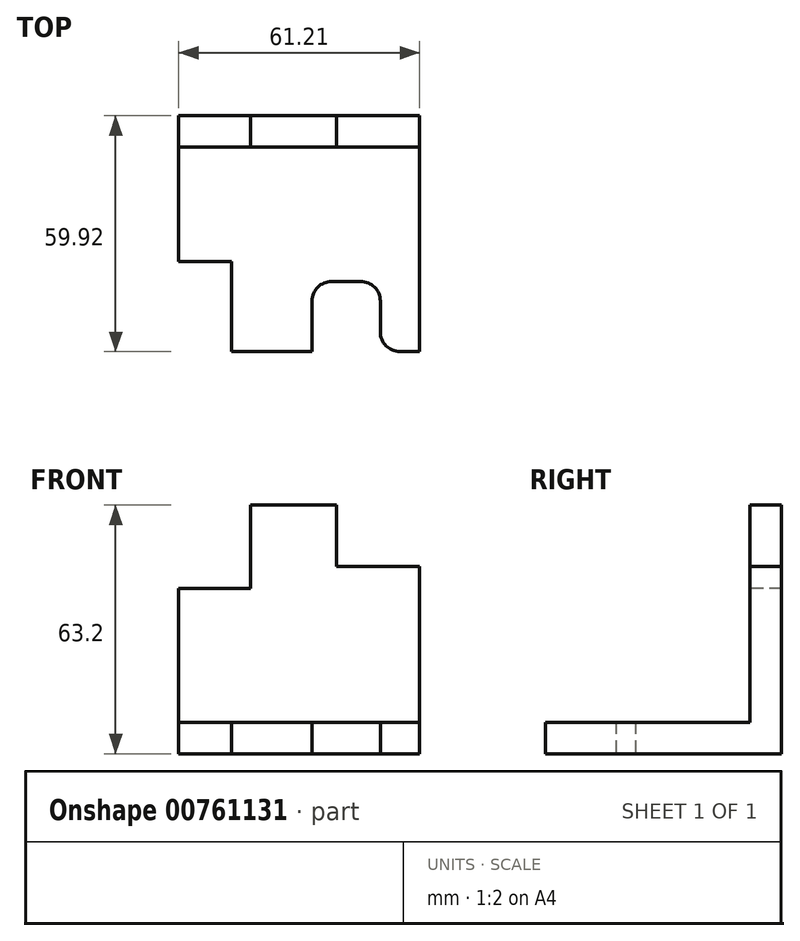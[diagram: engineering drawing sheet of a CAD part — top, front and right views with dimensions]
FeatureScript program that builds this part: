
annotation { "Feature Type Name" : "Feature", "Feature Type Description" : "" }
export const myFeature = defineFeature(function(context is Context, id is Id, definition is map)
    precondition{}
    {
        {
            var Q0;
            Q0=qCreatedBy(makeId("Top.planeOp"),FACE);
            var sketch = newSketch(context, id + "F0", { "sketchPlane" : qUnion([Q0])});
            skLineSegment(sketch, "E0", {"start": v(0, 0) * mm, "end": v(0, -29.06) * mm});
            skLineSegment(sketch, "E1", {"start": v(0, -29.06) * mm, "end": v(13.43, -29.06) * mm});
            skLineSegment(sketch, "E2", {"start": v(13.43, -29.06) * mm, "end": v(13.43, -51.92) * mm});
            skLineSegment(sketch, "E3", {"start": v(13.43, -51.92) * mm, "end": v(33.86, -51.92) * mm});
            skLineSegment(sketch, "E4", {"start": v(33.86, -51.92) * mm, "end": v(33.86, -39.1) * mm});
            skLineSegment(sketch, "E5", {"start": v(38.86, -34.1) * mm, "end": v(46.22, -34.1) * mm});
            skLineSegment(sketch, "E6", {"start": v(51.22, -39.1) * mm, "end": v(51.22, -46.92) * mm});
            skLineSegment(sketch, "E7", {"start": v(56.22, -51.92) * mm, "end": v(61.2, -51.92) * mm});
            skLineSegment(sketch, "E8", {"start": v(61.2, -51.92) * mm, "end": v(61.2, 0) * mm});
            skLineSegment(sketch, "E9", {"start": v(61.2, 0) * mm, "end": v(0, 0) * mm});
            skPoint(sketch, "E10.visualSharp", {"position": v(51.22, -34.1) * mm});
            skArc(sketch, "E10.filletArc", {"start": v(51.22, -39.1) * mm, "mid": v(49.76, -35.57) * mm, "end": v(46.22, -34.1) * mm});
            skPoint(sketch, "E11.visualSharp", {"position": v(33.86, -34.1) * mm});
            skArc(sketch, "E11.filletArc", {"start": v(38.86, -34.1) * mm, "mid": v(35.33, -35.57) * mm, "end": v(33.86, -39.1) * mm});
            skPoint(sketch, "E12.visualSharp", {"position": v(51.22, -51.92) * mm});
            skArc(sketch, "E12.filletArc", {"start": v(51.22, -46.92) * mm, "mid": v(52.69, -50.46) * mm, "end": v(56.22, -51.92) * mm});
            skSolve(sketch);
        }
        {
            var Q0;
            Q0=makeQuery(id+"F0.imprint","IMPRINT",FACE,{"disambiguationData":[TD([[makeQuery(id+"F0.imprint","IMPRINT",EDGE,{"derivedFrom":sQuery(id+"F0.wireOp",EDGE,"E0")}),1.0]])]});
            extrude(context, id + "F1", {"entities" : qUnion([Q0]), "depth" : 8 * mm, "offsetDistance" : 25 * mm});
        }
        {
            var Q0;
            Q0=qCreatedBy(makeId("Front.planeOp"),FACE);
            var sketch = newSketch(context, id + "F2", { "sketchPlane" : qUnion([Q0])});
            skLineSegment(sketch, "E13", {"start": v(0, 42) * mm, "end": v(18.28, 42) * mm});
            skLineSegment(sketch, "E14", {"start": v(18.28, 42) * mm, "end": v(18.28, 63.2) * mm});
            skLineSegment(sketch, "E15", {"start": v(18.28, 63.2) * mm, "end": v(40.03, 63.2) * mm});
            skLineSegment(sketch, "E16", {"start": v(40.03, 63.2) * mm, "end": v(40.03, 47.55) * mm});
            skLineSegment(sketch, "E17", {"start": v(40.03, 47.55) * mm, "end": v(61.2, 47.55) * mm});
            skLineSegment(sketch, "E18", {"start": v(61.2, 47.55) * mm, "end": v(61.2, 0) * mm});
            skLineSegment(sketch, "E19", {"start": v(61.2, 0) * mm, "end": v(0, 0) * mm});
            skLineSegment(sketch, "E20", {"start": v(0, 0) * mm, "end": v(0, 42) * mm});
            skSolve(sketch);
        }
        {
            var Q0;
            Q0 = qSketchRegion(id + "F2", true);
            extrude(context, id + "F3", {"entities" : qUnion([Q0]), "operationType" : NewBodyOperationType.ADD, "oppositeDirection" : true, "depth" : 8 * mm, "offsetDistance" : 25 * mm});
        }
    });
